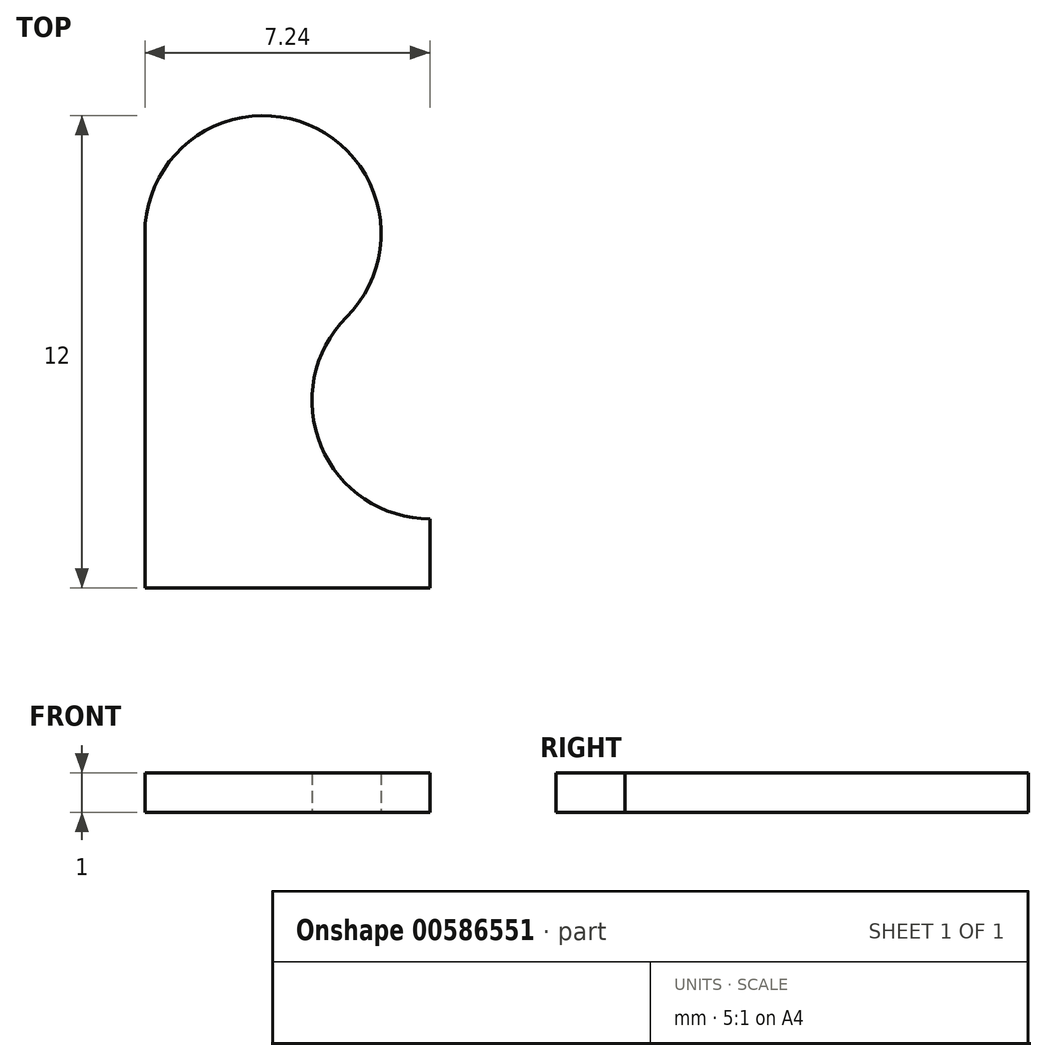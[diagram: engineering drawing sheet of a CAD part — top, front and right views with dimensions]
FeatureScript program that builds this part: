
annotation { "Feature Type Name" : "Feature", "Feature Type Description" : "" }
export const myFeature = defineFeature(function(context is Context, id is Id, definition is map)
    precondition{}
    {
        {
            var Q0;
            Q0=qCreatedBy(makeId("Top.planeOp"),FACE);
            var sketch = newSketch(context, id + "F0", { "sketchPlane" : qUnion([Q0])});
            skLineSegment(sketch, "E0", {"start": v(0, 0) * mm, "end": v(0, 9) * mm});
            skArc(sketch, "E1", {"start": v(0, 9) * mm, "mid": v(4.15, 11.77) * mm, "end": v(5.12, 6.88) * mm});
            skArc(sketch, "E2", {"start": v(5.12, 6.88) * mm, "mid": v(4.47, 3.6) * mm, "end": v(7.24, 1.76) * mm});
            skLineSegment(sketch, "E3", {"start": v(3, 9) * mm, "end": v(7.24, 4.76) * mm, "construction": true});
            skLineSegment(sketch, "E4", {"start": v(7.24, 0) * mm, "end": v(7.24, 4.76) * mm, "construction": true});
            skLineSegment(sketch, "E5", {"start": v(0, 0) * mm, "end": v(7.24, 0) * mm});
            skLineSegment(sketch, "E6", {"start": v(7.24, 1.76) * mm, "end": v(7.24, 0) * mm});
            skLineSegment(sketch, "E7", {"start": v(0, 9) * mm, "end": v(3, 9) * mm, "construction": true});
            skLineSegment(sketch, "E8", {"start": v(3, 9) * mm, "end": v(3, 6) * mm, "construction": true});
            skLineSegment(sketch, "E9", {"start": v(3, 6) * mm, "end": v(3, 3) * mm, "construction": true});
            skLineSegment(sketch, "E10", {"start": v(3, 0) * mm, "end": v(3, 3) * mm, "construction": true});
            skSolve(sketch);
        }
        {
            var Q0;
            Q0=qSketchRegion(id+"F0",true);
            extrude(context, id + "F1", {"entities" : qUnion([Q0]), "depth" : 1 * mm, "offsetDistance" : 25 * mm});
        }
    });
